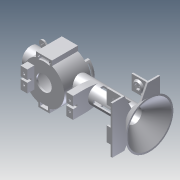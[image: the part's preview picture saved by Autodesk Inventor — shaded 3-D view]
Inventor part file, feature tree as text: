
AUTODESK INVENTOR PART (.ipt)
format: ipt  version: 2011 (Build 150239000, 239)  size: 731,136 bytes
history: native  units: mm
features: extrude x36, sketch x30, other x17, mirror x4, fillet x2, pattern_circular x1, draft x1, split x1, projected_geometry x1, plane x1
ambient origin geometry x8: Origin, YZ Plane, XZ Plane, XY Plane, X Axis, Y Axis, Z Axis, Center Point
bodies: Solid1 (feature_tree)
feature tree (94):
  other  "feeding wheel OD"
  extrude  "feeding wheel wTHK"  Depth=42.0mm
  other  "exit tube plane"
  extrude  "exit tube"  Depth=1.75mm
  extrude  "STR CUT01"  [1 undecoded]
  other  "feeding tube plane"
  extrude  "feeding tube"  TaperAngle=0.0deg  [1 undecoded]
  extrude  "STR CUT02"  Depth=15.0mm
  extrude  "feeding wheel back"  Depth=1.75mm
  extrude  "mounting hole"  Depth=10.0mm TaperAngle=0.0deg
  other  "refsketch"
  other  "support plane"
  other  "refsketch02"
  extrude  "servosupport01"  Depth=1.75mm
  other  "ref plane02"
  extrude  "servosupport02_1"  Depth=16.0mm
  extrude  "servosupport02_2"  TaperAngle=0.0deg  [1 undecoded]
  extrude  "STR mid hole cut"  Depth=10.0mm
  extrude  "Sensor Light Support"  Depth=33.8mm
  mirror  "Sensor Light support mirror"
  extrude  "STR cut03"  Depth=21.5mm
  extrude  "STR cut04"  TaperAngle=0.0deg  [1 undecoded]
  extrude  "Distance sensor support"  Depth=1.75mm
  extrude  "STR cut05"  Depth=13.1mm
  extrude  "STR cut06"  TaperAngle=0.0deg  [1 undecoded]
  extrude  "distance adjustment hole"  Depth=1.6mm
  extrude  "distance sensor back plate"  Depth=0.2mm
  extrude  "light sensor back plate"  Depth=1.75mm
  extrude  "checking hole big"  TaperAngle=0.0deg  [1 undecoded]
  extrude  "checking hole small"  TaperAngle=0.0deg  [1 undecoded]
  pattern_circular  "checking hole small pattern"  [2 undecoded]
  fillet  "servosupport fillet"  [1 undecoded]
  other  "led sketch plane"
  other  "led hole sketch"
  extrude  "led outer arc"  Depth=1.75mm
  extrude  "led support"  TaperAngle=0.0deg  [1 undecoded]
  extrude  "led hole"  Depth=1.75mm
  extrude  "servo mount cut"  TaperAngle=0.0deg  [1 undecoded]
  extrude  "wire feed support"  Depth=3.0mm
  other  "front wheel plane"
  other  "wire support"
  other  "wire top cut plane"
  extrude  "wire support extrude"  Depth=1.75mm
  mirror  "wire support mirror"
  extrude  "wire top cut"  Depth=3.5mm
  other  "wire support rails plane"
  extrude  "wire support rails extrude"  Depth=1.75mm
  fillet  "wire rails fillet"  Radius=1.75mm
  other  "Cut Plane Ref"
  other  "funnel catcher"
  sketch  "Sketch44"  dims[d103=7.62mm]
  other  "tube center plane"
  extrude  "mount vertical fin"  TaperAngle=0.0deg  [1 undecoded]
  extrude  "mount support"  Depth=5.0mm
  sketch  "Sketch46"  dims[d106=1.75mm]
  extrude  "mount support hole"  Depth=5.0mm
  other  "rib plane"
  extrude  "Extrusion49"  Depth=3.5mm
  extrude  "Extrusion50"  Depth=1.75mm
  draft  "FaceDraft1"
  mirror  "Mirror9"
  mirror  "Mirror10"
  extrude  "mount center cut"  TaperAngle=0.0deg  [1 undecoded]
  split  "Split1"
  sketch  "Sketch4"  dims[d5=26.75mm d6=42.0mm]
  sketch  "Sketch5"  dims[d7=90.0deg d9=1.75mm]
  sketch  "Sketch6"  dims[d10=10.0mm d11=0.0mm d12=-31.0mm]
  sketch  "Sketch7"  dims[d15=1.75mm d16=0.0mm d17=0.0mm]
  sketch  "Sketch8"  dims[d18=10.0mm d19=0.0mm d21=15.0mm]
  sketch  "Sketch9"  dims[d22=76.0mm d23=1.75mm]
  sketch  "Sketch10"  dims[d24=15.0mm d25=10.0mm d26=0.0mm]
  sketch  "Sketch11"  dims[d27=10.0mm d28=0.0mm d29=1.75mm]
  sketch  "Sketch14"  dims[d30=0.0mm d31=16.0mm]
  sketch  "Sketch17"  dims[d32=1.75mm d33=0.0mm]
  sketch  "Sketch18"  dims[d35=13.5mm d36=10.0mm]
  sketch  "Sketch20"  dims[d37=2.2mm d38=33.8mm]
  sketch  "Sketch24"  dims[d39=7.0mm d40=21.5mm]
  sketch  "Sketch25"  dims[d42=1.75mm d43=0.0mm]
  sketch  "Sketch26"  dims[d44=0.0mm d45=0.0mm d46=1.75mm]
  sketch  "Sketch28"  dims[d47=0.0mm d64=13.1mm]
  sketch  "Sketch29"  dims[d65=1.75mm d66=0.0mm]
  sketch  "Sketch30"  dims[d82=12.7mm d83=1.6mm]
  sketch  "Sketch31"  dims[d84=0.2mm d87=0.2mm]
  sketch  "Sketch32"  dims[d88=1.75mm d89=1.75mm]
  sketch  "Sketch34"  dims[d90=1.75mm d91=0.0mm]
  projected_geometry  "Projected Loop1"
  sketch  "Sketch35"  dims[d94=1.75mm d95=0.0mm]
  sketch  "Sketch36"  dims[d98=8.02mm]
  sketch  "Sketch37"  dims[d99=1.75mm]
  plane  "Work Plane11"
  sketch  "Sketch40"  dims[d100=0.0mm]
  sketch  "Sketch41"  dims[d102=1.6mm]
  sketch  "Sketch45"  dims[d105=0.0mm]
  sketch  "Sketch49"  dims[d107=1.75mm d108=1.75mm d109=0.0mm d110=1.75mm d111=0.0mm d120=1.75mm d121=0.0mm d122=3.0mm d124=1.75mm d128=3.5mm d129=1.75mm d130=1.75mm d131=0.0mm d132=5.0mm d133=5.0mm d134=3.5mm d135=1.75mm d136=0.0mm d137=5.0mm d138=5.0mm d139=3.5mm d140=1.75mm d141=0.0mm d142=30.0mm d143=-31.415927mm d145=50.0mm d146=10.0mm d147=90.0deg d148=45.0deg d149=1.75mm d150=0.0mm d151=-9.0mm d152=6.8mm d153=25.275mm d154=45.0deg d157=1.75mm d158=0.0mm d159=1.75mm d160=0.0mm d161=0.8mm d162=40.0mm d164=1.25mm d165=10.0mm d167=10.0mm d169=1.75mm d170=0.0mm d171=7.2mm d172=1.75mm d173=0.0mm d174=21.75mm d175=0.0mm d176=1.5mm d177=0.7mm d180=1.75mm d181=1.75mm d182=1.7mm d183=2.4mm d184=2.4mm d185=4.3mm d186=0.0mm d187=1.5mm d188=3.0mm d189=22.0mm d190=0.0mm d192=13.375mm d201=-55.0mm d209=1.75mm d210=6.981317mm d211=4.75mm d212=0.0mm d213=1.75mm d214=1.75mm d215=1.75mm d216=2.0mm d217=4.75mm d218=0.0mm d219=1.0mm d220=1.0mm d221=0.0mm d222=0.5mm d230=1.75mm d231=15.0mm d232=9.25mm d242=12.0mm d243=1.75mm d246=15.0mm d247=0.0mm d252=1.75mm d253=0.0mm d256=1.75mm d257=45.0deg d258=3.0mm d259=1.75mm d260=0.0mm d267=-1.5mm d273=5.0mm d274=5.0mm d275=1.0mm d276=1.75mm d277=0.0mm d278=5.3mm d279=1.5mm d280=0.75mm d281=0.0mm d282=1.55mm d283=0.0mm d284=45.0deg]
note: 14 required parameter values undecoded (feature->parameter linkage not recoverable at this tier; creation-order binding heuristic only, values carry confidence <= 0.55)
